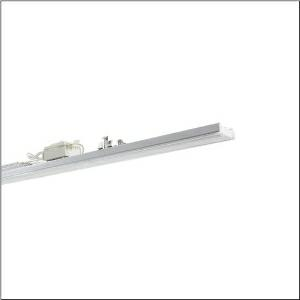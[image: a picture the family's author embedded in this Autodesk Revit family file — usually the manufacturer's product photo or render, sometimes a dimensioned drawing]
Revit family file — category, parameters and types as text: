
# Revit family: licross_r__21_recessed_mo_51te18vn48xg_56d6
name_source: partatom
category: Lighting Fixtures
units: mm (PartAtom-declared; Revit-internal decimal feet)

## family parameters
Cut with Voids When Loaded = No
Host = Face
Light Source = No
Part Type = Normal
Room Calculation Point = No
Round Connector Dimension = Use Diameter
Shared = No

## types (1)
- --- (1 x LED, 8000 lm, 44.7 W, 4000K)
    Apparent Load = 45 VA
    CIE Flux Codes = 83 96 99 100 100
    Color Rendering = 80
    Color Temperature = 4000K
    Default Elevation = 1800 mm
    Description = Licross® 21 Recessed MO, luminaire insert, of sheet steel, galvanised, coil coated, white, length: 1.500mm, width: 66mm, height: 67mm, LED rated luminous flux: 8.000lm, light colour: 840, control gear: DALI 2, CLO, with plug, 5-pole, with phase selection, mains connection: 220..240V, AC, 50/60Hz, start of lifetime: 45W, end of service life: 49W, internal wiring halogen-free, primary light control with lens, of plastic, primary optical cover: cover, of PMMA, light emission: direct distribution, primary light characteristic: symmetric, protection rating (complete): IP54, insulation class (complete): insulation class I (protective earthing), certification: CE, ENEC, VDE, UKCA, protection symbol: D if used in an environment with non-conductive dust loads with corresponding accessories, impact resistance: IK06, permissible ambient temperature for indoor applications: -25..+35°C, corresponds to IFS (International Featured Standards) requirements for safety and quality in the food industry, reducing of maximum allowable ambient temperature of 5°C with ceiling mounting, LABS conformity tested according to VDMA 24364:2018-05, packaging unit: 1 piece
    Height = 58 mm
    Lamp = 1 x LED
    Lamp Light Flux = 8000 lm
    Lamp Power = 44.7 W
    Lamp count = 1
    Length = 1500 mm
    Luminous efficacy = 179 lm/W
    Manufacturer = Siteco
    ModVariant = No
    Model = 51TE18VN48XG
    Mounting Place = Ceiling
    Mounting Type = Pendant
    Number of Poles = 1
    OnlyDefault = Yes
    Power Factor = 1
    Product Name = Licross® 21 Recessed MO
    Product group = luminaire insert | ceiling pendant
    ProductGroupID = 902
    Protection Class = Protection class I
    Protection Degree = IP 54
    RLX_Detail_Level = 1
    RLX_Emergency_Light_Flux = 0 lm
    RLX_Emergency_Type = 0
    RLX_Emergency_Type_DB = No
    RlxData = <blob elided: 24633 chars, md5=434e3a96>
    Socket = socket
    Standby Power = 0 W
    System Light Flux = 8000 lm
    System Power = 45 W
    Type Comments = factory setting: luminous flux: 100 % | dim-lin: 254 | 299 mA
    Type Image = l_1296930.jpg
    URL = http://relux.com
    VarID = @adj_108529
    Voltage = 0 V
    Weight = 0.00 kg
    Width = 66 mm

## geometry (parser evidence)
native form markers: Blend x4, Sweep x9
no freeform markers — native parametric forms only
